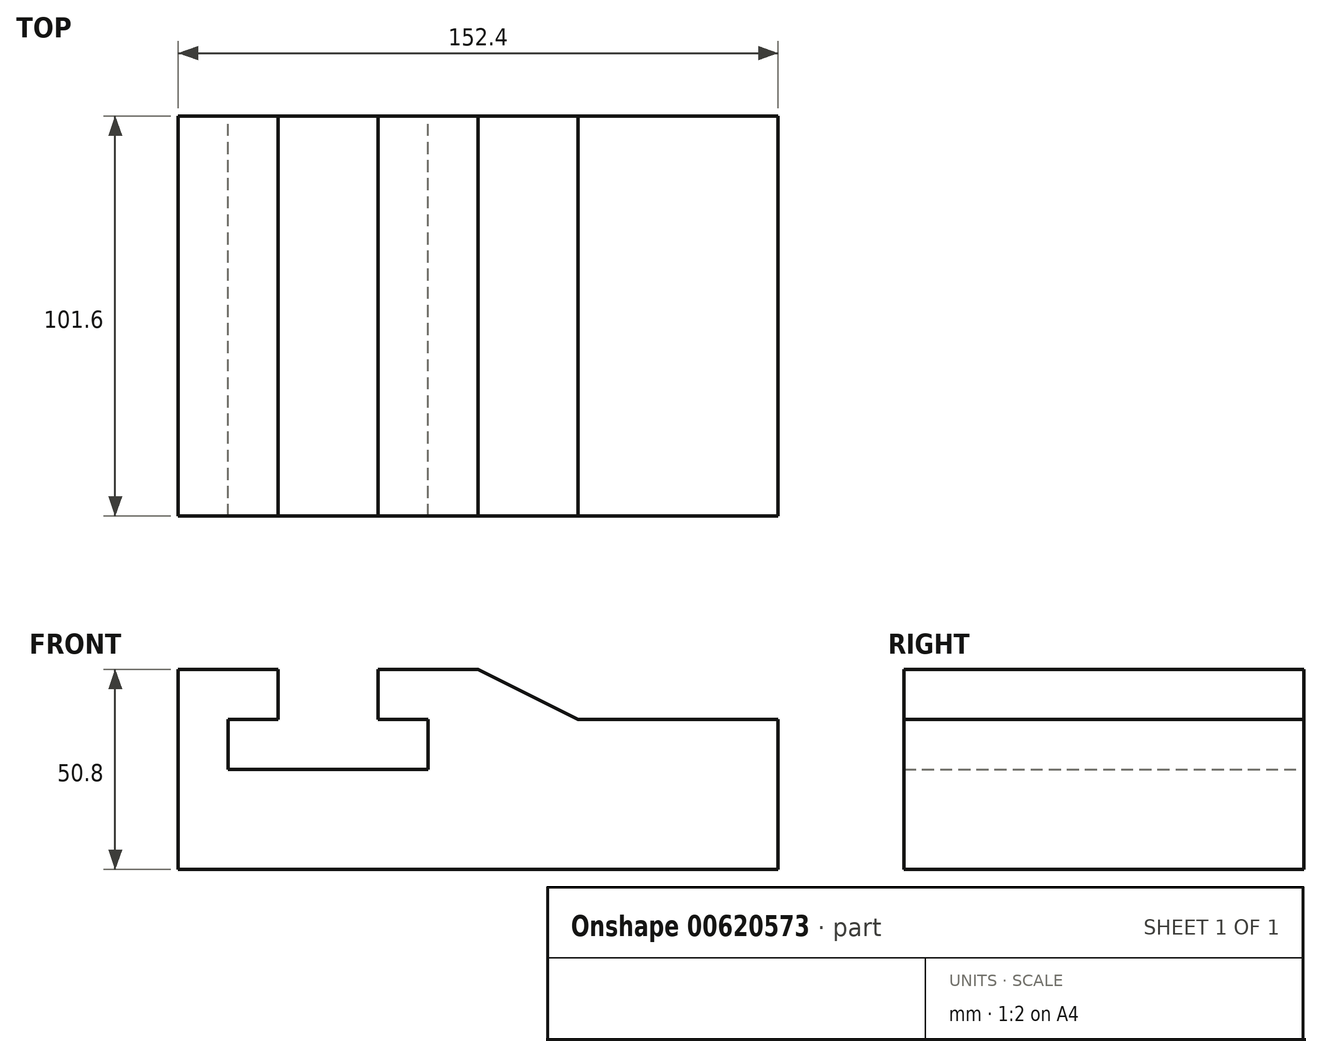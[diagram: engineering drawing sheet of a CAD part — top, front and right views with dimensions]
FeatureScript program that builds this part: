
annotation { "Feature Type Name" : "Feature", "Feature Type Description" : "" }
export const myFeature = defineFeature(function(context is Context, id is Id, definition is map)
    precondition{}
    {
        {
            var Q0;
            Q0=qCreatedBy(makeId("Front.planeOp"),FACE);
            var sketch = newSketch(context, id + "F0", { "sketchPlane" : qUnion([Q0])});
            skLineSegment(sketch, "E0", {"start": v(209.77, -77.99) * mm, "end": v(362.17, -77.99) * mm});
            skLineSegment(sketch, "E1", {"start": v(209.77, -77.99) * mm, "end": v(209.77, -27.19) * mm});
            skLineSegment(sketch, "E2", {"start": v(209.77, -27.19) * mm, "end": v(235.17, -27.19) * mm});
            skLineSegment(sketch, "E3", {"start": v(235.17, -27.19) * mm, "end": v(235.17, -39.89) * mm});
            skLineSegment(sketch, "E4", {"start": v(235.17, -39.89) * mm, "end": v(222.47, -39.89) * mm});
            skLineSegment(sketch, "E5", {"start": v(222.47, -39.89) * mm, "end": v(222.47, -52.59) * mm});
            skLineSegment(sketch, "E6", {"start": v(222.47, -52.59) * mm, "end": v(273.27, -52.59) * mm});
            skLineSegment(sketch, "E7", {"start": v(273.27, -52.59) * mm, "end": v(273.27, -39.89) * mm});
            skLineSegment(sketch, "E8", {"start": v(273.27, -39.89) * mm, "end": v(260.57, -39.89) * mm});
            skLineSegment(sketch, "E9", {"start": v(260.57, -39.89) * mm, "end": v(260.57, -27.19) * mm});
            skLineSegment(sketch, "E10", {"start": v(260.57, -27.19) * mm, "end": v(285.97, -27.19) * mm});
            skLineSegment(sketch, "E11", {"start": v(362.17, -77.99) * mm, "end": v(362.17, -39.89) * mm});
            skLineSegment(sketch, "E12", {"start": v(362.17, -39.89) * mm, "end": v(311.37, -39.89) * mm});
            skLineSegment(sketch, "E13", {"start": v(285.97, -27.19) * mm, "end": v(311.37, -39.89) * mm});
            skSolve(sketch);
        }
        {
            var Q0;
            Q0 = qSketchRegion(id + "F0", true);
            extrude(context, id + "F1", {"entities" : qUnion([Q0]), "depth" : 101.6 * mm, "offsetDistance" : 25.4 * mm});
        }
    });
